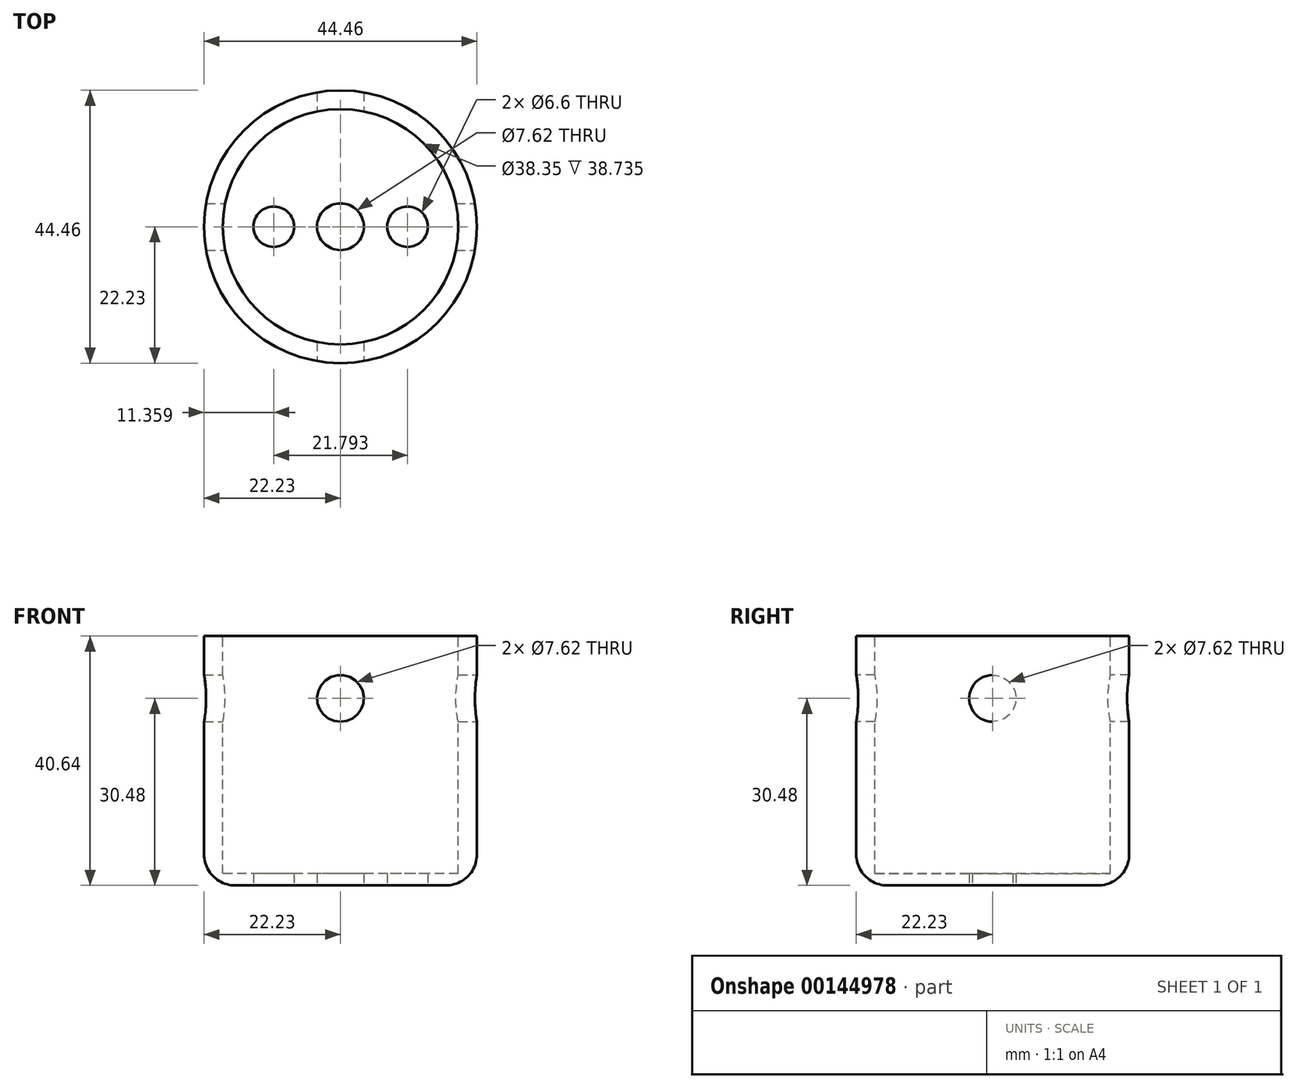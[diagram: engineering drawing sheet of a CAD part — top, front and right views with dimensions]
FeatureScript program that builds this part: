
annotation { "Feature Type Name" : "Feature", "Feature Type Description" : "" }
export const myFeature = defineFeature(function(context is Context, id is Id, definition is map)
    precondition{}
    {
        {
            var Q0;
            Q0=qCreatedBy(makeId("Top.planeOp"),FACE);
            var sketch = newSketch(context, id + "F0", { "sketchPlane" : qUnion([Q0])});
            skCircle(sketch, "E0", {"center": v(0, 0) * mm, "radius": 22.23 * mm});
            skSolve(sketch);
        }
        {
            var Q0;
            Q0=qSketchRegion(id+"F0",true);
            extrude(context, id + "F1", {"entities" : qUnion([Q0]), "oppositeDirection" : true, "depth" : 40.64 * mm});
        }
        {
            var Q0;
            Q0=makeQuery(id+"F1.opExtrude","CAP_FACE",FACE,{"disambiguationData":[OSD([sQuery(id+"F0.wireOp",EDGE,"E0")])],"isStart":false});
            var sketch = newSketch(context, id + "F2", { "sketchPlane" : qUnion([Q0])});
            skCircle(sketch, "E1", {"center": v(0, 0) * mm, "radius": 3.8 * mm});
            skSolve(sketch);
        }
        {
            var Q0;
            Q0=qSketchRegion(id+"F2",true);
            extrude(context, id + "F3", {"entities" : qUnion([Q0]), "operationType" : NewBodyOperationType.REMOVE, "endBound" : BoundingType.THROUGH_ALL, "oppositeDirection" : true, "depth" : 38.1 * mm});
        }
        {
            var Q0;
            Q0=qCreatedBy(makeId("Right.planeOp"),FACE);
            var sketch = newSketch(context, id + "F4", { "sketchPlane" : qUnion([Q0])});
            skLineSegment(sketch, "E2", {"start": v(0, 0) * mm, "end": v(0, -74.59) * mm, "construction": true});
            skCircle(sketch, "E3", {"center": v(0, -10.16) * mm, "radius": 3.81 * mm});
            skSolve(sketch);
        }
        {
            var Q0;
            Q0=qSketchRegion(id+"F4",true);
            extrude(context, id + "F5", {"entities" : qUnion([Q0]), "operationType" : NewBodyOperationType.REMOVE, "endBound" : BoundingType.THROUGH_ALL, "oppositeDirection" : true, "depth" : 25.4 * mm, "hasSecondDirection" : true, "secondDirectionBound" : SecondDirectionBoundingType.THROUGH_ALL, "secondDirectionOppositeDirection" : false, "secondDirectionDepth" : 25.4 * mm});
        }
        {
            var Q0;
            Q0=qCreatedBy(makeId("Front.planeOp"),FACE);
            var sketch = newSketch(context, id + "F6", { "sketchPlane" : qUnion([Q0])});
            skLineSegment(sketch, "E4", {"start": v(0, 0) * mm, "end": v(0, -36.04) * mm, "construction": true});
            skCircle(sketch, "E5", {"center": v(0, -10.16) * mm, "radius": 3.81 * mm});
            skSolve(sketch);
        }
        {
            var Q0;
            Q0=qSketchRegion(id+"F6",true);
            extrude(context, id + "F7", {"entities" : qUnion([Q0]), "operationType" : NewBodyOperationType.REMOVE, "endBound" : BoundingType.THROUGH_ALL, "oppositeDirection" : true, "depth" : 25.4 * mm, "hasSecondDirection" : true, "secondDirectionBound" : SecondDirectionBoundingType.THROUGH_ALL, "secondDirectionOppositeDirection" : false, "secondDirectionDepth" : 25.4 * mm});
        }
        {
            var Q0;
            Q0=makeQuery(id+"F1.opExtrude","CAP_FACE",FACE,{"disambiguationData":[OSD([sQuery(id+"F0.wireOp",EDGE,"E0")])],"isStart":false});
            var sketch = newSketch(context, id + "F8", { "sketchPlane" : qUnion([Q0])});
            skCircle(sketch, "E6", {"center": v(10.92, 0) * mm, "radius": 3.3 * mm});
            skCircle(sketch, "E7", {"center": v(-10.87, 0) * mm, "radius": 3.3 * mm});
            skSolve(sketch);
        }
        {
            var Q0;
            Q0=qSketchRegion(id+"F8",true);
            extrude(context, id + "F9", {"entities" : qUnion([Q0]), "operationType" : NewBodyOperationType.REMOVE, "endBound" : BoundingType.THROUGH_ALL, "oppositeDirection" : true, "depth" : 31.86 * mm});
        }
        {
            var Q0;
            Q0=makeQuery(id+"F1.opExtrude","CAP_FACE",FACE,{"disambiguationData":[OSD([sQuery(id+"F0.wireOp",EDGE,"E0")])],"isStart":true});
            var sketch = newSketch(context, id + "F10", { "sketchPlane" : qUnion([Q0])});
            skCircle(sketch, "E8", {"center": v(0, 0) * mm, "radius": 19.18 * mm});
            skSolve(sketch);
        }
        {
            var Q0;
            Q0=qSketchRegion(id+"F10",true);
            extrude(context, id + "F11", {"entities" : qUnion([Q0]), "operationType" : NewBodyOperationType.REMOVE, "oppositeDirection" : true, "depth" : 38.73 * mm});
        }
        {
            var Q0;
            Q0=makeQuery(id+"F1.opExtrude","CAP_EDGE",EDGE,{"disambiguationData":[OSD([sQuery(id+"F0.wireOp",EDGE,"E0")])],"isStart":false});
            fillet(context, id + "F12", {"entities" : qUnion([Q0]), "radius" : 5.08 * mm, "tangentPropagation" : true, "allowEdgeOverflow" : false});
        }
    });
